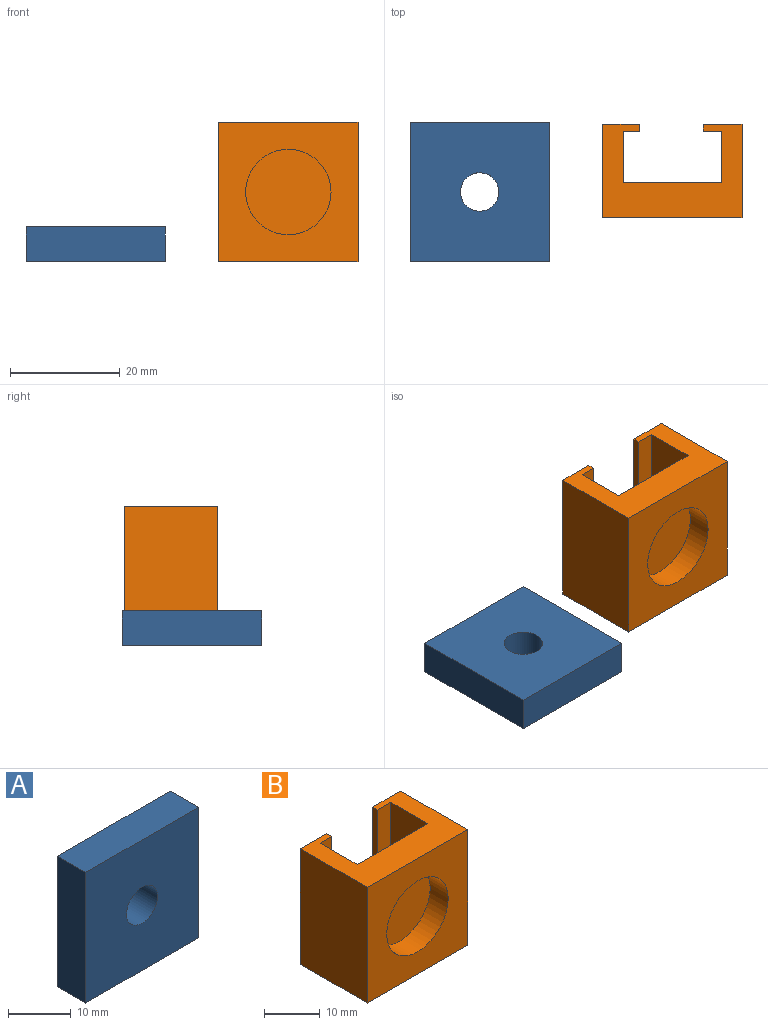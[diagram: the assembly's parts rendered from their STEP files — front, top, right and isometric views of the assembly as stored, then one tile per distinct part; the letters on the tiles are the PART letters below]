
ASSEMBLY  parts=2 mates=1
PART A: 7 faces, bbox 25.4x6.4x25.4 mm
  f0: plane 25.4x6.35mm, normal (-1,0,0), area 161.3mm2, adj f1,f3,f4,f6
  f1: plane 25.4x6.35mm, normal (0,0,1), area 161.3mm2, adj f0,f2,f4,f6
  f2: plane 25.4x6.35mm, normal (1,0,0), area 161.3mm2, adj f1,f3,f4,f6
  f3: plane 25.4x6.35mm, normal (0,0,-1), area 161.3mm2, adj f0,f2,f4,f6
  f4: plane 25.4x25.4mm, normal (0,-1,0), area 606.7mm2, adj f0,f1,f2,f3,f5
  f5: cylinder r=3.5mm len=7mm, axis (0,-1,0), area 139.6mm2, adj f4,f6
  f6: plane 25.4x25.4mm, normal (0,1,0), area 606.7mm2, adj f0,f1,f2,f3,f5
PART B: 16 faces, bbox 25.4x17x25.4 mm
  f0: plane 25.4x16.99mm, normal (0,0,-1), area 248.6mm2, adj f1,f3,f4,f5,f6,f7,f8,f9
  f1: plane 25.4x16.99mm, normal (1,0,0), area 431.4mm2, adj f0,f2,f10,f13
  f2: plane 25.4x16.99mm, normal (0,0,1), area 248.6mm2, adj f1,f3,f4,f5,f6,f7,f8,f9
  f3: plane 25.4x16.99mm, normal (-1,0,0), area 431.4mm2, adj f0,f2,f5,f13
  f4: plane 25.4x1.27mm, normal (1,0,0), area 32.3mm2, adj f0,f2,f5,f12
  f5: plane 25.4x6.68mm, normal (0,1,0), area 169.8mm2, adj f0,f2,f3,f4
  f6: plane 25.4x9.37mm, normal (1,0,0), area 237.9mm2, adj f0,f2,f8,f12
  f7: plane 25.4x9.37mm, normal (-1,0,0), area 237.9mm2, adj f0,f2,f8,f11
  f8: plane 25.4x17.95mm, normal (0,1,0), area 455.8mm2, adj f0,f2,f6,f7
  f9: plane 25.4x1.27mm, normal (-1,0,0), area 32.3mm2, adj f0,f2,f10,f11
  f10: plane 25.4x7.08mm, normal (0,1,0), area 179.9mm2, adj f0,f1,f2,f9
  f11: plane 25.4x3.36mm, normal (0,-1,0), area 85.2mm2, adj f0,f2,f7,f9
  f12: plane 25.4x2.96mm, normal (0,-1,0), area 75.1mm2, adj f0,f2,f4,f6
  f13: plane 25.4x25.4mm, normal (0,-1,0), area 454.7mm2, adj f0,f1,f2,f3,f14
  f14: cylinder r=7.79mm len=15.57mm, axis (0,-1,0), area 223.7mm2, adj f13,f15
  f15: plane 15.57x15.57mm, normal (0,-1,0), area 190.5mm2, adj f14
PLACE A rot(axis=(-1,0,0),90deg) t=(-4.31,9.59,-21.49)mm
PLACE B t=(30.82,4.88,-8.79)mm
MATE planar A.f5 <-> B.f0  axis (0,0,-1) through (-4.31,9.59,-21.49)mm
